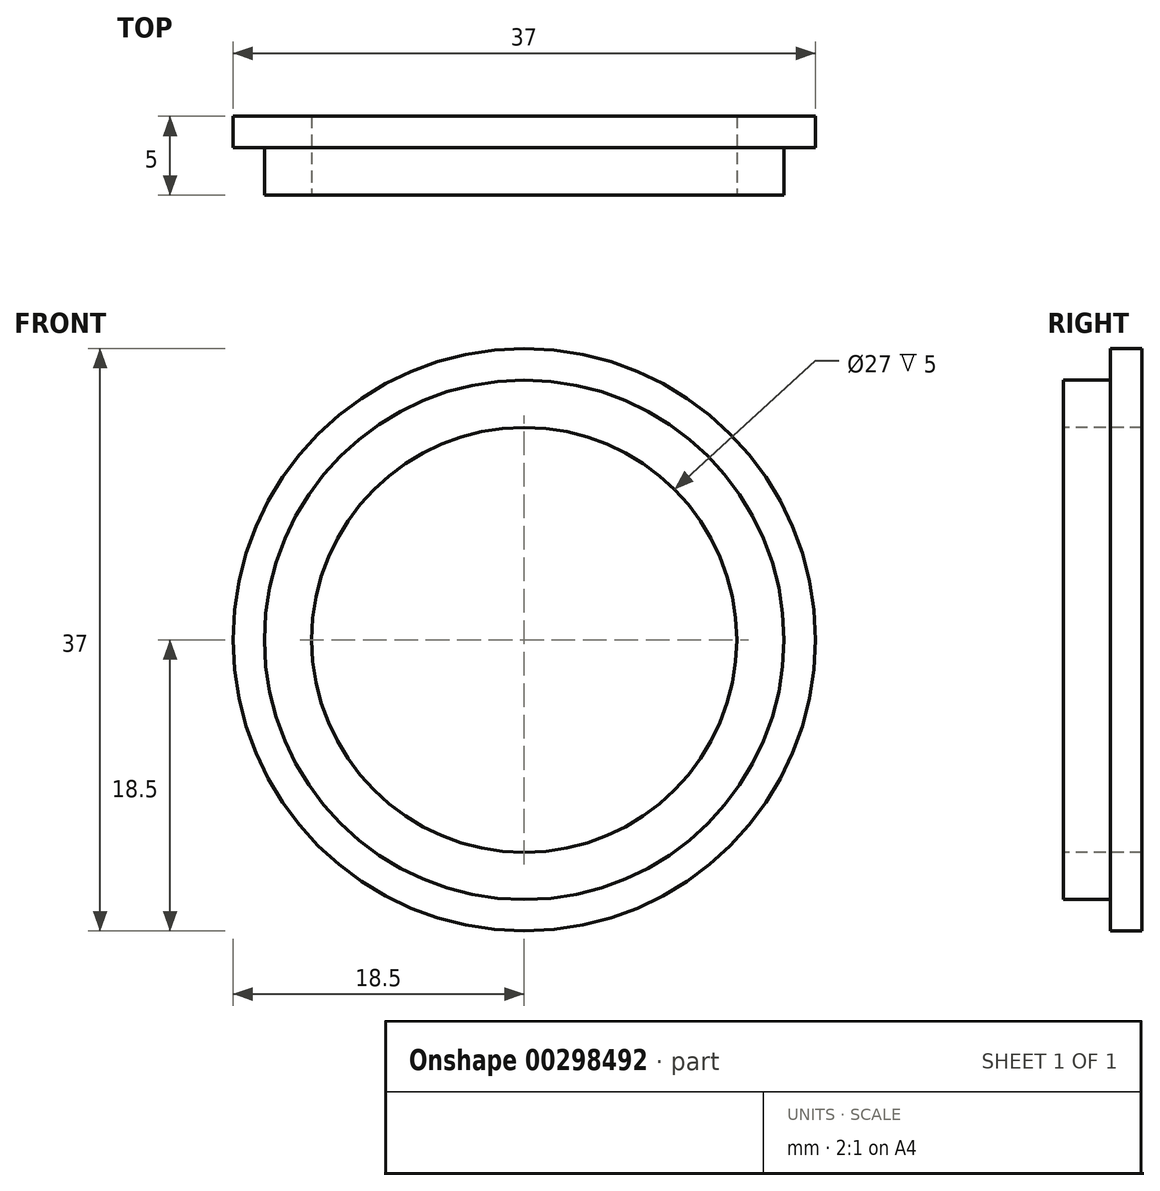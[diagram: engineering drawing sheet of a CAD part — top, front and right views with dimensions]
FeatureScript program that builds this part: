
annotation { "Feature Type Name" : "Feature", "Feature Type Description" : "" }
export const myFeature = defineFeature(function(context is Context, id is Id, definition is map)
    precondition{}
    {
        {
            var Q0;
            Q0=qCreatedBy(makeId("Top.planeOp"),FACE);
            var sketch = newSketch(context, id + "F0", { "sketchPlane" : qUnion([Q0])});
            skLineSegment(sketch, "E0.bottom", {"start": v(13.5, 0) * mm, "end": v(16.5, 0) * mm, "construction": true});
            skLineSegment(sketch, "E0.top", {"start": v(13.5, -3) * mm, "end": v(16.5, -3) * mm});
            skLineSegment(sketch, "E0.left", {"start": v(13.5, 0) * mm, "end": v(13.5, -3) * mm});
            skLineSegment(sketch, "E0.right", {"start": v(16.5, 0) * mm, "end": v(16.5, -3) * mm});
            skLineSegment(sketch, "E1.top", {"start": v(13.5, 2) * mm, "end": v(18.5, 2) * mm});
            skLineSegment(sketch, "E1.left", {"start": v(13.5, 0) * mm, "end": v(13.5, 2) * mm});
            skLineSegment(sketch, "E1.right", {"start": v(18.5, 0) * mm, "end": v(18.5, 2) * mm});
            skLineSegment(sketch, "E2", {"start": v(0, 0) * mm, "end": v(0, 3.04) * mm});
            skLineSegment(sketch, "E3", {"start": v(16.5, 0) * mm, "end": v(18.5, 0) * mm});
            skSolve(sketch);
        }
        {
            var Q0;
            Q0 = qSketchRegion(id + "F0", true);
            var Q1;
            Q1=sQuery(id+"F0.wireOp",EDGE,"E2");
            revolve(context, id + "F1", {"entities" : qUnion([Q0]), "axis" : qUnion([Q1]), "revolveType" : RevolveType.FULL});
        }
    });
